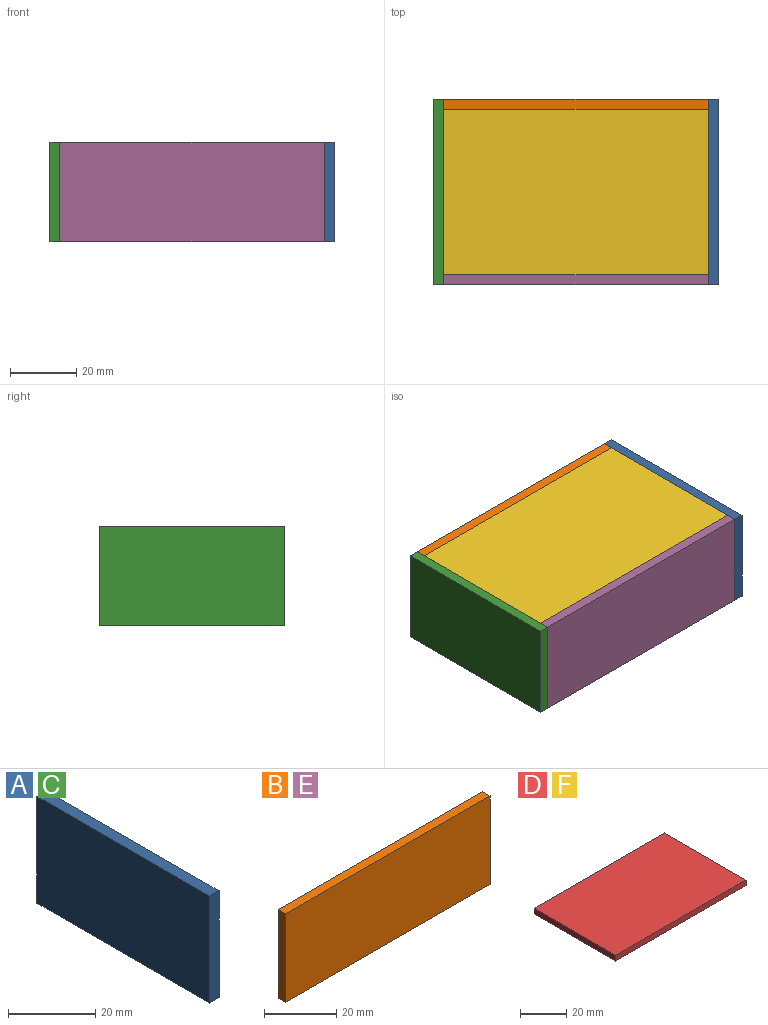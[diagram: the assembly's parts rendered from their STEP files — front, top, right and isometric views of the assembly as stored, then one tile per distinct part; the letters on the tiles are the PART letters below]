
ASSEMBLY  parts=6 mates=11
PART A: 6 faces, bbox 3x56x30 mm
  f0: plane 30x3mm, normal (0,-1,0), area 90mm2, adj f1,f3,f4,f5
  f1: plane 56x3mm, normal (0,0,-1), area 168mm2, adj f0,f2,f4,f5
  f2: plane 30x3mm, normal (0,1,0), area 90mm2, adj f1,f3,f4,f5
  f3: plane 56x3mm, normal (0,0,1), area 168mm2, adj f0,f2,f4,f5
  f4: plane 56x30mm, normal (1,0,0), area 1680mm2, adj f0,f1,f2,f3
  f5: plane 56x30mm, normal (-1,0,0), area 1680mm2, adj f0,f1,f2,f3
PART B: 6 faces, bbox 80x3x30 mm
  f0: plane 30x3mm, normal (-1,0,0), area 90mm2, adj f1,f3,f4,f5
  f1: plane 80x3mm, normal (0,0,-1), area 240mm2, adj f0,f2,f4,f5
  f2: plane 30x3mm, normal (1,0,0), area 90mm2, adj f1,f3,f4,f5
  f3: plane 80x3mm, normal (0,0,1), area 240mm2, adj f0,f2,f4,f5
  f4: plane 80x30mm, normal (0,-1,0), area 2400mm2, adj f0,f1,f2,f3
  f5: plane 80x30mm, normal (0,1,0), area 2400mm2, adj f0,f1,f2,f3
PART C: same geometry as A
PART D: 6 faces, bbox 80x50x3 mm
  f0: plane 50x3mm, normal (-1,0,0), area 150mm2, adj f1,f3,f4,f5
  f1: plane 80x3mm, normal (0,-1,0), area 240mm2, adj f0,f2,f4,f5
  f2: plane 50x3mm, normal (1,0,0), area 150mm2, adj f1,f3,f4,f5
  f3: plane 80x3mm, normal (0,1,0), area 240mm2, adj f0,f2,f4,f5
  f4: plane 80x50mm, normal (0,0,1), area 4000mm2, adj f0,f1,f2,f3
  f5: plane 80x50mm, normal (0,0,-1), area 4000mm2, adj f0,f1,f2,f3
PART E: same geometry as B
PART F: same geometry as D
PLACE A t=(73.33,-54.74,-1.94)mm
PLACE B t=(-6.67,1.26,-1.94)mm
PLACE C t=(-9.67,-54.74,-1.94)mm
PLACE D t=(-6.67,-51.74,-1.94)mm
PLACE E t=(-6.67,-51.74,-1.94)mm
PLACE F t=(-6.67,-51.74,25.06)mm
MATE fastened B.f4 <-> D.f3  axis (0,-1,0) through (73.33,-1.74,-1.94)mm
MATE fastened B.f2 <-> A.f5  axis (1,0,0) through (73.33,1.26,28.06)mm
MATE parallel E.f4 <-> F.f1  axis (0,-1,0) through (33.33,-54.74,13.06)mm
MATE parallel F.f3 <-> B.f4  axis (0,1,0) through (73.33,-1.74,28.06)mm
MATE parallel E.f5 <-> F.f1  axis (0,1,0) through (-6.67,-51.74,28.06)mm
MATE fastened E.f0 <-> C.f4  axis (-1,0,0) through (-6.67,-54.74,28.06)mm
MATE fastened F.f3 <-> B.f4  axis (0,1,0) through (73.33,-1.74,28.06)mm
MATE parallel E.f5 <-> B.f4  axis (0,1,0) through (73.33,-51.74,28.06)mm
MATE fastened E.f5 <-> F.f1  axis (0,1,0) through (73.33,-51.74,28.06)mm
MATE parallel F.f4 <-> F.f4  axis (0,0,1) through (-6.67,-26.74,28.06)mm
MATE parallel E.f4 <-> F.f1  axis (0,-1,0) through (33.33,-54.74,13.06)mm
